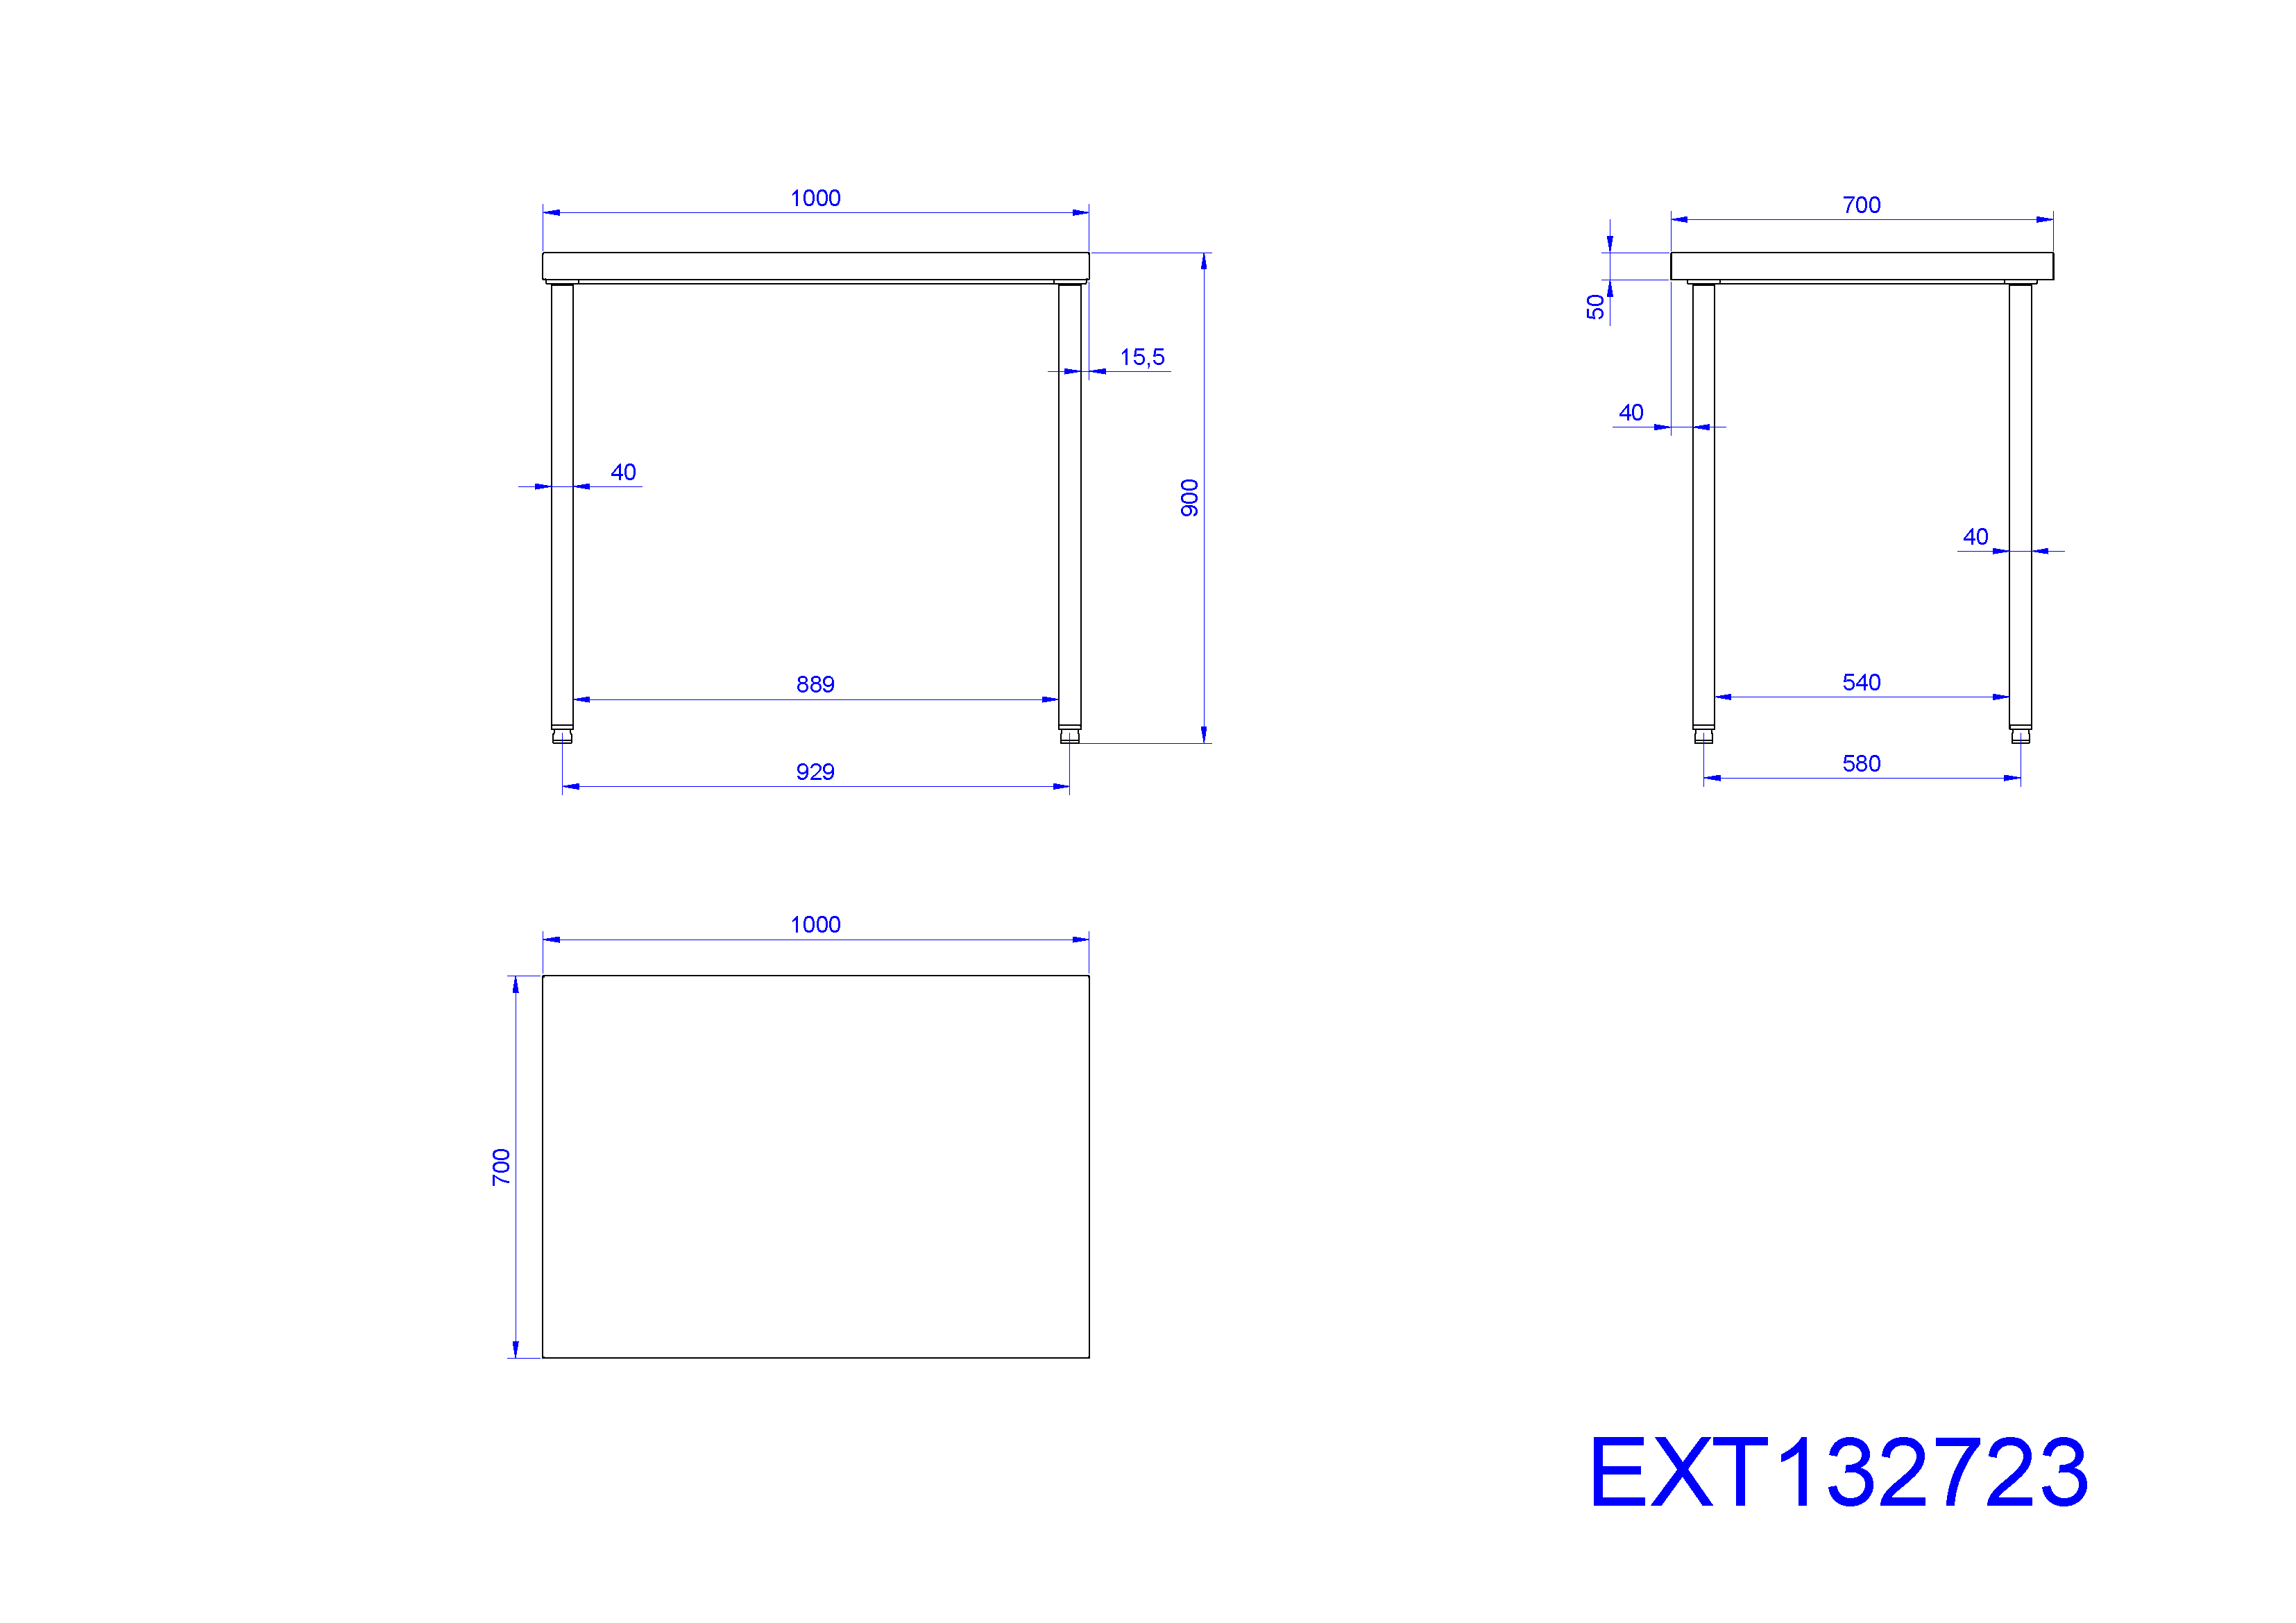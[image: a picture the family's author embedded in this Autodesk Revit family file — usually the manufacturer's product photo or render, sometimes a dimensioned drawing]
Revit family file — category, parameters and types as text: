
# Revit family: QF_ELECTROLUXPROFESSIONAL_132842_WTD1607N
name_source: partatom
category: Attrezzature speciali
units: mm (PartAtom-declared; Revit-internal decimal feet)

## family parameters
Basato su piano di lavoro = No
Condiviso = No
Punto di calcolo locali = No
Quota connettore circolare = Usa diametro
Sempre verticale = Sì
Taglio con vuoti quando caricato = No
Tipo di parte = Normale

## types (1)
- Standard
    Accessory = Sì
    Cold Water Size = 0 mm
    Compressed Air Pressure = 0.0 Pa
    Compressed Air Size = 0 mm
    Compressed Air Volume = 0.0 L/s
    Condensate Return Size = 0 mm
    Cycle = 0 Hz
    Depth Actual = 700 mm  [stored 2.29659 ft]
    Descrizione = WORK TABLE-DISASSEMBLED 1600MM
    Direct Waste Size = 0 mm
    Gas Input Pressure = 0
    Gas KW = 0
    Gas Size = 0 mm
    HP = 0 HP
    Height Actual = 900 mm  [stored 2.95276 ft]
    Hot Water Size = 0 mm
    Item Number = 132842
    Length Actual = 1600 mm  [stored 5.24934 ft]
    Modello = WTD1607N
    Phase = 0
    Produttore = Electrolux Professional
    Prospetto di default = 0 mm  [stored 0 ft]
    Refrigerant Compressor Remote = Sì
    Refrigeration Liquid Line Size = 0 mm  [stored 0 ft]
    Refrigeration Suction Line Size = 0 mm  [stored 0 ft]
    Steam Consumption per Hour = 0
    Steam Supply Maximum Pressure = 0.0 Pa
    Steam Supply Minimum Pressure = 0.0 Pa
    Steam Supply Size = 0 mm
    URL = https://www.electroluxprofessional.com
    URL Manufacturer = https://www.electroluxprofessional.com
    Volts = 0 V
    Watts = 0 W
    Weight = 53.00 kg

note: source unit labels omitted for Gas Input Pressure — the stored unit's dimension contradicts the parameter name (converter mislabeling)

note: [stored X ft] marks values corroborated as IEEE doubles in the binary element streams (Revit-internal decimal feet)

## geometry (parser evidence)
native form markers: Sweep x2
no freeform markers — native parametric forms only
